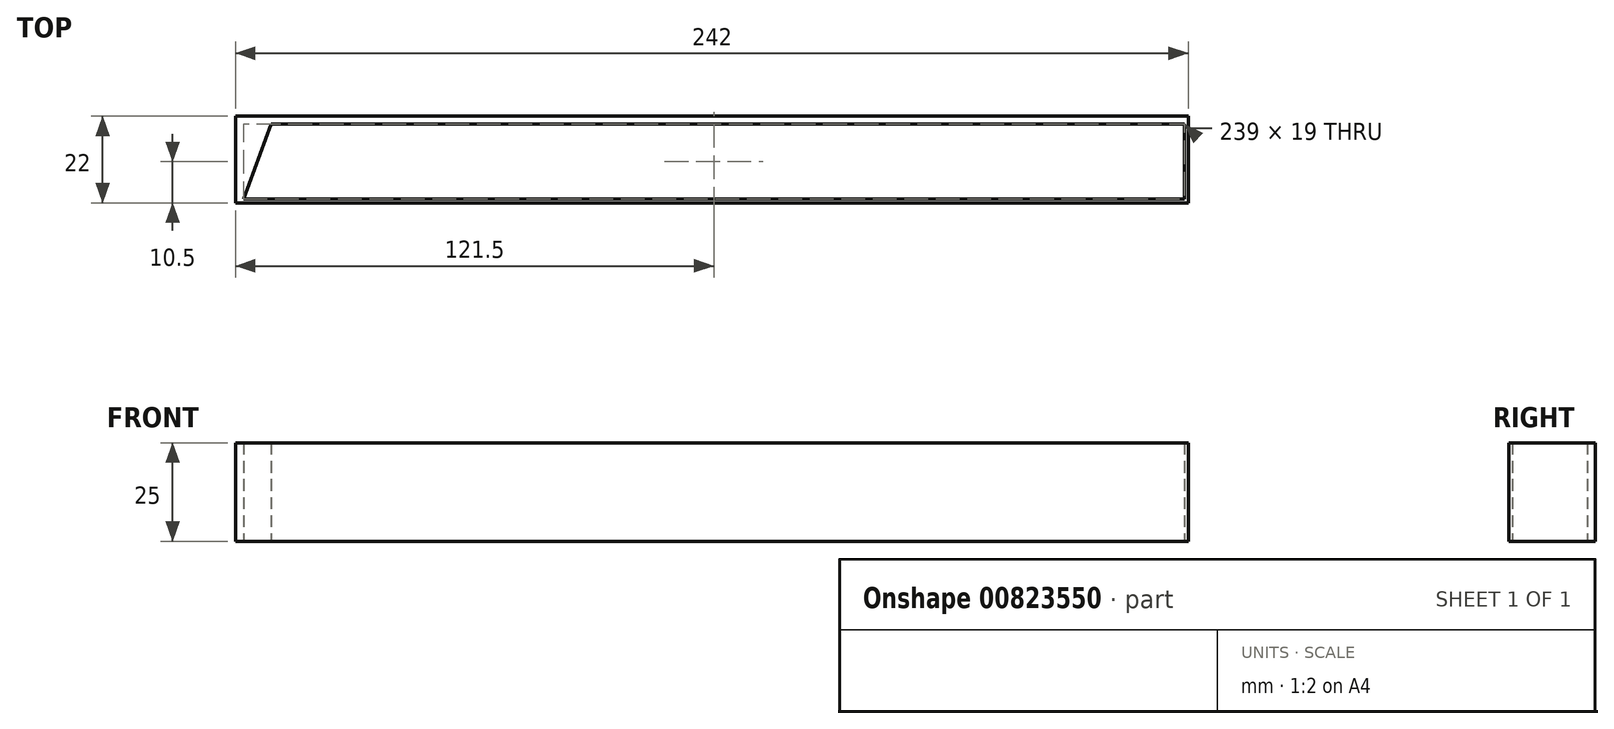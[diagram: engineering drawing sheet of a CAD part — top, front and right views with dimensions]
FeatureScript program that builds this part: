
annotation { "Feature Type Name" : "Feature", "Feature Type Description" : "" }
export const myFeature = defineFeature(function(context is Context, id is Id, definition is map)
    precondition{}
    {
        {
            var Q0;
            Q0=qCreatedBy(makeId("Top.planeOp"),FACE);
            var sketch = newSketch(context, id + "F0", { "sketchPlane" : qUnion([Q0])});
            skLineSegment(sketch, "E0.bottom", {"start": v(-120, 10) * mm, "end": v(120, 10) * mm});
            skLineSegment(sketch, "E0.top", {"start": v(-120, -10) * mm, "end": v(120, -10) * mm});
            skLineSegment(sketch, "E0.left", {"start": v(-120, 10) * mm, "end": v(-120, -10) * mm});
            skLineSegment(sketch, "E0.right", {"start": v(120, 10) * mm, "end": v(120, -10) * mm});
            skPoint(sketch, "E0.middle", {"position": v(0, 0) * mm});
            skLineSegment(sketch, "E1", {"start": v(-119, -10) * mm, "end": v(-112, 9) * mm});
            skLineSegment(sketch, "E2.bottom", {"start": v(-121, 11) * mm, "end": v(121, 11) * mm});
            skLineSegment(sketch, "E2.top", {"start": v(-121, -11) * mm, "end": v(121, -11) * mm});
            skLineSegment(sketch, "E2.left", {"start": v(-121, 11) * mm, "end": v(-121, -11) * mm});
            skLineSegment(sketch, "E2.right", {"start": v(121, 11) * mm, "end": v(121, -11) * mm});
            skLineSegment(sketch, "E3", {"start": v(-120, 9) * mm, "end": v(-112, 9) * mm});
            skLineSegment(sketch, "E4", {"start": v(-120, 9) * mm, "end": v(120, 9) * mm});
            skLineSegment(sketch, "E5", {"start": v(-112, 9) * mm, "end": v(-86.46, 9) * mm});
            skLineSegment(sketch, "E6", {"start": v(-86.46, 9) * mm, "end": v(120, 9) * mm});
            skSolve(sketch);
        }
        {
            var Q0;
            {var subQ4=sQuery(id+"F0.wireOp",EDGE,"E0.bottom");Q0=makeQuery(id+"F0.imprint","IMPRINT",FACE,{"disambiguationData":[TD([[makeQuery(id+"F0.imprint","IMPRINT",EDGE,{"derivedFrom":subQ4}),1.0]])]});}
            var Q1;
            {var subQ2=sQuery(id+"F0.wireOp",EDGE,"E0.bottom");Q1=makeQuery(id+"F0.imprint","IMPRINT",FACE,{"disambiguationData":[TD([[makeQuery(id+"F0.imprint","IMPRINT",EDGE,{"derivedFrom":subQ2}),-1.0]])]});}
            var Q2;
            {var subQ3=sQuery(id+"F0.wireOp",EDGE,"E1");Q2=makeQuery(id+"F0.imprint","IMPRINT",FACE,{"disambiguationData":[TD([[makeQuery(id+"F0.imprint","IMPRINT",EDGE,{"derivedFrom":subQ3}),1.0]])]});}
            extrude(context, id + "F1", {"entities" : qUnion([Q0, Q1, Q2]), "depth" : 25 * mm, "offsetDistance" : 25 * mm});
        }
    });
